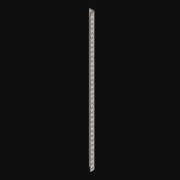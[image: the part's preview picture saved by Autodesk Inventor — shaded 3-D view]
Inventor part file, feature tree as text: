
AUTODESK INVENTOR PART (.ipt)
format: ipt  version: 2021 (Build 250183000, 183)  size: 1,335,296 bytes
history: native  units: in
note: dims shown in document units (in); Inventor stores cm internally (conversion verified against a paired STEP export)
features: extrude x70, other x68, sketch x4, pattern_linear x2, sheet_metal_op x1
ambient origin geometry x8: Origin, YZ Plane, XZ Plane, XY Plane, X Axis, Y Axis, Z Axis, Center Point
bodies: Solid1 (feature_tree)
feature tree (145):
  pattern_linear  "Rectangular Pattern1"  Spacing1=0.5in  [1 undecoded]
  pattern_linear  "Rectangular Pattern3"  Count1=34  [1 undecoded]
  extrude  "Extrusion1"  Depth=0.5in
  extrude  "Extrusion2"  Depth=0.5in
  sketch  "Sketch1"  dims[d0=0.182in]
  other  "Srf1"
  sketch  "Sketch3"  dims[d1=0.063in d2=0.0in]
  other  "Srf3"
  other  "Srf4"
  other  "Srf5"
  other  "Srf6"
  other  "Srf7"
  other  "Srf8"
  other  "Srf9"
  other  "Srf10"
  other  "Srf11"
  other  "Srf12"
  other  "Srf13"
  other  "Srf14"
  other  "Srf15"
  other  "Srf16"
  other  "Srf17"
  other  "Srf18"
  other  "Srf19"
  other  "Srf20"
  other  "Srf21"
  other  "Srf22"
  other  "Srf23"
  other  "Srf24"
  other  "Srf25"
  other  "Srf26"
  other  "Srf27"
  other  "Srf28"
  other  "Srf29"
  other  "Srf30"
  other  "Srf31"
  other  "Srf32"
  other  "Srf33"
  other  "Srf34"
  other  "Srf35"
  other  "Srf36"
  other  "Srf142"
  other  "Srf143"
  other  "Srf144"
  other  "Srf145"
  other  "Srf146"
  other  "Srf147"
  other  "Srf148"
  other  "Srf149"
  other  "Srf150"
  other  "Srf151"
  other  "Srf152"
  other  "Srf153"
  other  "Srf154"
  other  "Srf155"
  other  "Srf156"
  other  "Srf157"
  other  "Srf158"
  other  "Srf159"
  other  "Srf160"
  other  "Srf161"
  other  "Srf162"
  other  "Srf163"
  other  "Srf164"
  other  "Srf165"
  other  "Srf166"
  other  "Srf167"
  other  "Srf168"
  other  "Srf169"
  other  "Srf170"
  other  "Srf171"
  other  "Srf172"
  other  "Srf173"
  other  "Srf174"
  sketch  "Sketch4"  dims[d6=0.182in]
  sketch  "Sketch5"  dims[d7=0.063in d8=0.0in d11=0.5in d12=0.3937in d14=0.5in d18=13.3858in d20=0.5in d21=0.5in d22=0.0in d23=0.841in d24=0.0in]
  sheet_metal_op  "Fold1"
  extrude  "ExtrusionSrf1"  TaperAngle=0.0deg  [1 undecoded]
  extrude  "ExtrusionSrf3"  Depth=0.5in TaperAngle=0.0deg
  extrude  "ExtrusionSrf4"  [1 undecoded]
  extrude  "ExtrusionSrf5"  [1 undecoded]
  extrude  "ExtrusionSrf6"  [1 undecoded]
  extrude  "ExtrusionSrf7"  [1 undecoded]
  extrude  "ExtrusionSrf8"  [1 undecoded]
  extrude  "ExtrusionSrf9"  [1 undecoded]
  extrude  "ExtrusionSrf10"  [1 undecoded]
  extrude  "ExtrusionSrf11"  [1 undecoded]
  extrude  "ExtrusionSrf12"  [1 undecoded]
  extrude  "ExtrusionSrf13"  [1 undecoded]
  extrude  "ExtrusionSrf14"  [1 undecoded]
  extrude  "ExtrusionSrf15"  [1 undecoded]
  extrude  "ExtrusionSrf16"  [1 undecoded]
  extrude  "ExtrusionSrf17"  [1 undecoded]
  extrude  "ExtrusionSrf18"  [1 undecoded]
  extrude  "ExtrusionSrf19"  [1 undecoded]
  extrude  "ExtrusionSrf20"  [1 undecoded]
  extrude  "ExtrusionSrf21"  [1 undecoded]
  extrude  "ExtrusionSrf22"  [1 undecoded]
  extrude  "ExtrusionSrf23"  [1 undecoded]
  extrude  "ExtrusionSrf24"  [1 undecoded]
  extrude  "ExtrusionSrf25"  [1 undecoded]
  extrude  "ExtrusionSrf26"  [1 undecoded]
  extrude  "ExtrusionSrf27"  [1 undecoded]
  extrude  "ExtrusionSrf28"  [1 undecoded]
  extrude  "ExtrusionSrf29"  [1 undecoded]
  extrude  "ExtrusionSrf30"  [1 undecoded]
  extrude  "ExtrusionSrf31"  [1 undecoded]
  extrude  "ExtrusionSrf32"  [1 undecoded]
  extrude  "ExtrusionSrf33"  [1 undecoded]
  extrude  "ExtrusionSrf34"  [1 undecoded]
  extrude  "ExtrusionSrf35"  [1 undecoded]
  extrude  "ExtrusionSrf36"  [1 undecoded]
  extrude  "ExtrusionSrf142"  [1 undecoded]
  extrude  "ExtrusionSrf143"  [1 undecoded]
  extrude  "ExtrusionSrf144"  [1 undecoded]
  extrude  "ExtrusionSrf145"  [1 undecoded]
  extrude  "ExtrusionSrf146"  [1 undecoded]
  extrude  "ExtrusionSrf147"  [1 undecoded]
  extrude  "ExtrusionSrf148"  [1 undecoded]
  extrude  "ExtrusionSrf149"  [1 undecoded]
  extrude  "ExtrusionSrf150"  [1 undecoded]
  extrude  "ExtrusionSrf151"  [1 undecoded]
  extrude  "ExtrusionSrf152"  [1 undecoded]
  extrude  "ExtrusionSrf153"  [1 undecoded]
  extrude  "ExtrusionSrf154"  [1 undecoded]
  extrude  "ExtrusionSrf155"  [1 undecoded]
  extrude  "ExtrusionSrf156"  [1 undecoded]
  extrude  "ExtrusionSrf157"  [1 undecoded]
  extrude  "ExtrusionSrf158"  [1 undecoded]
  extrude  "ExtrusionSrf159"  [1 undecoded]
  extrude  "ExtrusionSrf160"  [1 undecoded]
  extrude  "ExtrusionSrf161"  [1 undecoded]
  extrude  "ExtrusionSrf162"  [1 undecoded]
  extrude  "ExtrusionSrf163"  [1 undecoded]
  extrude  "ExtrusionSrf164"  [1 undecoded]
  extrude  "ExtrusionSrf165"  [1 undecoded]
  extrude  "ExtrusionSrf166"  [1 undecoded]
  extrude  "ExtrusionSrf167"  [1 undecoded]
  extrude  "ExtrusionSrf168"  [1 undecoded]
  extrude  "ExtrusionSrf169"  [1 undecoded]
  extrude  "ExtrusionSrf170"  [1 undecoded]
  extrude  "ExtrusionSrf171"  [1 undecoded]
  extrude  "ExtrusionSrf172"  [1 undecoded]
  extrude  "ExtrusionSrf173"  [1 undecoded]
  extrude  "ExtrusionSrf174"  [1 undecoded]
note: 69 required parameter values undecoded (feature->parameter linkage not recoverable at this tier; creation-order binding heuristic only, values carry confidence <= 0.55)
